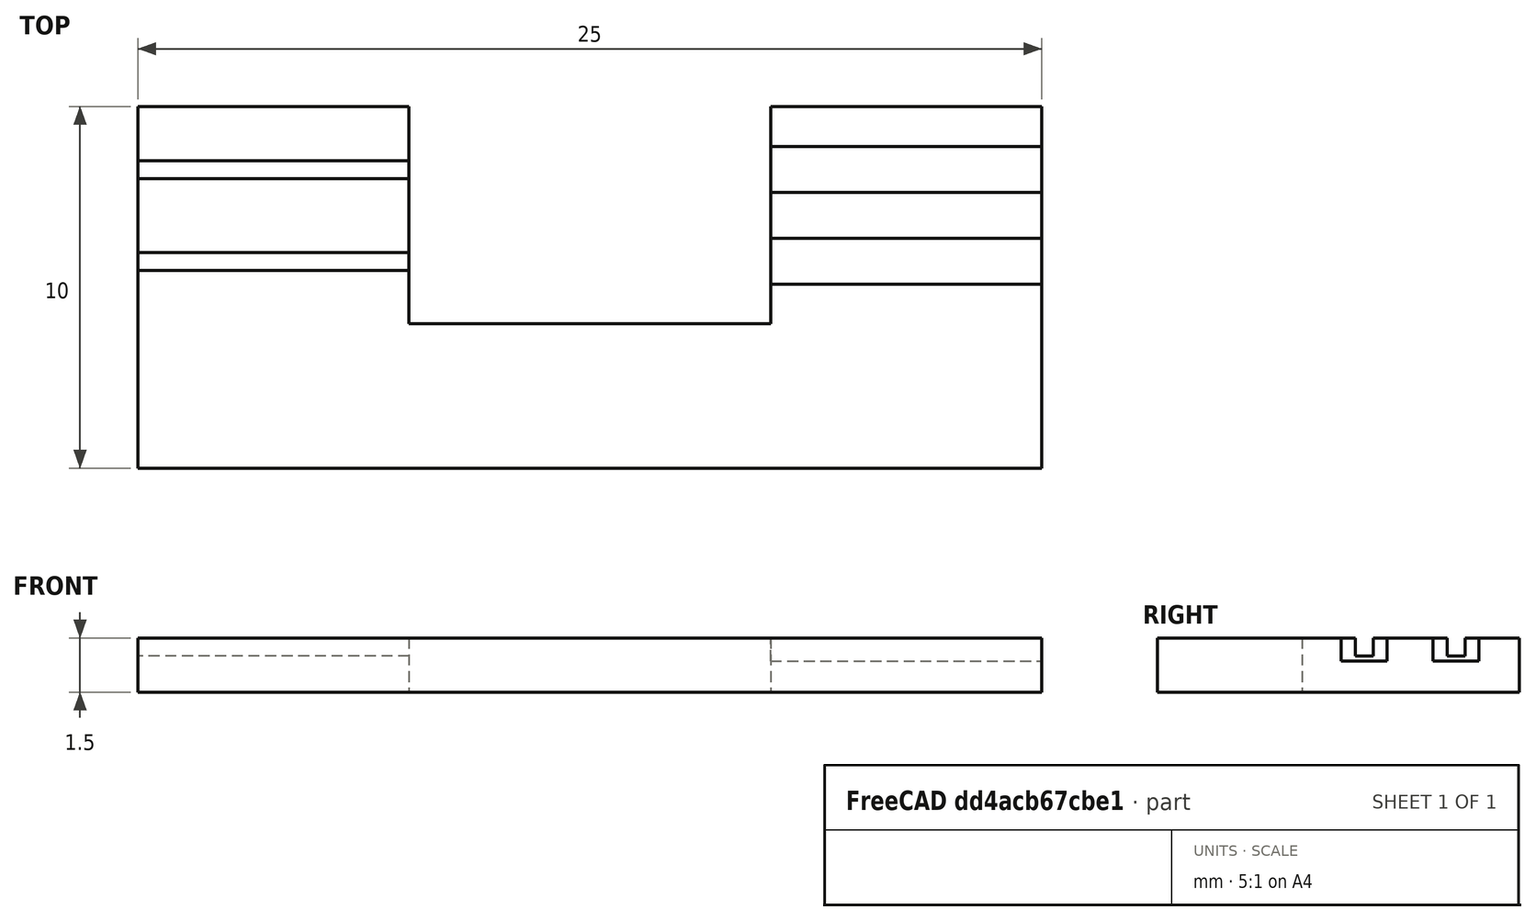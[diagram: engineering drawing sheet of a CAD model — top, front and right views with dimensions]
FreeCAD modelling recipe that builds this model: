
FCSTD DOCUMENT  (FreeCAD 0.18R16146 (Git))
Label: wire-jig
License: All rights reserved
LicenseURL: http://en.wikipedia.org/wiki/All_rights_reserved
objects: Sketcher::SketchObject×3, PartDesign::Pocket×2, PartDesign::Pad×1, PartDesign::Body×1
note: 10 computed .brp shape members not serialized (recipe doc carries the construction recipe); baked Part::Feature solids carry a one-line shape summary decoded from their .brp

FEATURE [Sketcher::SketchObject] Sketch
  MapMode = 5
  Support = -> [XY_Plane]
  sketch-geometry (8):
    g0: LineSegment StartX=-12.5 StartY=6 StartZ=0 EndX=-5 EndY=6 EndZ=0
    g1: LineSegment StartX=12.5 StartY=6 StartZ=0 EndX=12.5 EndY=-4 EndZ=0
    g2: LineSegment StartX=12.5 StartY=-4 StartZ=0 EndX=-12.5 EndY=-4 EndZ=0
    g3: LineSegment StartX=-12.5 StartY=-4 StartZ=0 EndX=-12.5 EndY=6 EndZ=0
    g4: LineSegment StartX=-5 StartY=6 StartZ=0 EndX=-5 EndY=0 EndZ=0
    g5: LineSegment StartX=-5 StartY=0 StartZ=0 EndX=5 EndY=0 EndZ=0
    g6: LineSegment StartX=5 StartY=0 StartZ=0 EndX=5 EndY=6 EndZ=0
    g7: LineSegment StartX=5 StartY=6 StartZ=0 EndX=12.5 EndY=6 EndZ=0
  constraints (22):
    c: Coincident(g7,g1)
    c: Coincident(g1,g2)
    c: Coincident(g2,g3)
    c: Coincident(g3,g0)
    c: Horizontal(g2)
    c: Vertical(g3)
    c: Symmetric(g0,g7,g-2)
    c: Vertical(g4)
    c: Coincident(g4,g5)
    c: Horizontal(g5)
    c: Coincident(g5,g6)
    c: Vertical(g6)
    c: PointOnObject(g5,g-1)
    c: Coincident(g0,g4)
    c: Tangent(g0,g7)
    c: Coincident(g6,g7)
    c: Equal(g0,g7)
    c: DistanceX(g0,g6) = 10
    c: Distance(g2) = 25
    c: Vertical(g1)
    c: Distance(g1) = 10
    c: DistanceY(g2,g4) = 4
FEATURE [PartDesign::Pad] Pad
  Length = 1.5
  Length2 = 100
  Profile = -> Sketch
  Reversed = true
  Type = 0
FEATURE [Sketcher::SketchObject] Sketch001
  MapMode = 5
  Support = -> [XY_Plane]
  sketch-geometry (11):
    g0: LineSegment StartX=-13.1646 StartY=4.50644 StartZ=0 EndX=-3.3788 EndY=4.50644 EndZ=0
    g1: LineSegment StartX=-3.3788 StartY=4.50644 StartZ=0 EndX=-3.3788 EndY=4.00644 EndZ=0
    g2: LineSegment StartX=-3.3788 StartY=4.00644 StartZ=0 EndX=-13.1646 EndY=4.00644 EndZ=0
    g3: LineSegment StartX=-13.1646 StartY=4.00644 StartZ=0 EndX=-13.1646 EndY=4.50644 EndZ=0
    g4: LineSegment StartX=-13.1646 StartY=1.96644 StartZ=0 EndX=-3.3788 EndY=1.96644 EndZ=0
    g5: LineSegment StartX=-3.3788 StartY=1.96644 StartZ=0 EndX=-3.3788 EndY=1.46644 EndZ=0
    g6: LineSegment StartX=-3.3788 StartY=1.46644 StartZ=0 EndX=-13.1646 EndY=1.46644 EndZ=0
    g7: LineSegment StartX=-13.1646 StartY=1.46644 StartZ=0 EndX=-13.1646 EndY=1.96644 EndZ=0
    g8: LineSegment StartX=3.29453 StartY=3.62144 StartZ=0 EndX=13.0803 EndY=3.62144 EndZ=0
    g9: LineSegment [constr] StartX=-13.9476 StartY=4.25644 StartZ=0 EndX=13.9476 EndY=4.25644 EndZ=0
    g10: LineSegment [constr] StartX=13.9476 StartY=1.71644 StartZ=0 EndX=-13.9476 EndY=1.71644 EndZ=0
  constraints (27):
    c: Coincident(g0,g1)
    c: Coincident(g1,g2)
    c: Coincident(g2,g3)
    c: Coincident(g3,g0)
    c: Horizontal(g0)
    c: Horizontal(g2)
    c: Vertical(g1)
    c: Coincident(g4,g5)
    c: Coincident(g5,g6)
    c: Coincident(g6,g7)
    c: Coincident(g7,g4)
    c: Horizontal(g4)
    c: Vertical(g5)
    c: Vertical(g7)
    c: Horizontal(g8)
    c: Equal(g3,g7)
    c: Symmetric(g9,g9,g-2)
    c: Vertical(g10,g9)
    c: Equal(g10,g9)
    c: Symmetric(g4,g6,g10)
    c: Symmetric(g2,g0,g9)
    c: Equal(g1,g5)
    c: Equal(g2,g4)
    c: Vertical(g4,g1)
    c: Equal(g2,g8)
    c: Distance(g3) = 0.5
    c: DistanceY(g10,g9) = 2.54
FEATURE [PartDesign::Body] Body
  Group = -> [Sketch,Pad,Sketch001,Sketch002,Pocket001,Pocket]
  Origin = -> Origin
  Tip = -> Pocket
FEATURE [Sketcher::SketchObject] Sketch002
  ExternalGeometry = -> [Pocket]
  MapMode = 5
  Support = -> [XY_Plane]
  sketch-geometry (10):
    g0: LineSegment StartX=13.4356 StartY=4.89144 StartZ=0 EndX=3.64684 EndY=4.89144 EndZ=0
    g1: LineSegment StartX=3.64684 StartY=4.89144 StartZ=0 EndX=3.64684 EndY=3.62144 EndZ=0
    g2: LineSegment StartX=3.64684 StartY=3.62144 StartZ=0 EndX=13.4356 EndY=3.62144 EndZ=0
    g3: LineSegment StartX=13.4356 StartY=3.62144 StartZ=0 EndX=13.4356 EndY=4.89144 EndZ=0
    g4: LineSegment StartX=13.4356 StartY=2.35144 StartZ=0 EndX=3.64684 EndY=2.35144 EndZ=0
    g5: LineSegment StartX=3.64684 StartY=2.35144 StartZ=0 EndX=3.64684 EndY=1.08144 EndZ=0
    g6: LineSegment StartX=3.64684 StartY=1.08144 StartZ=0 EndX=13.4356 EndY=1.08144 EndZ=0
    g7: LineSegment StartX=13.4356 StartY=1.08144 StartZ=0 EndX=13.4356 EndY=2.35144 EndZ=0
    g8: LineSegment [constr] StartX=-13.9476 StartY=4.25644 StartZ=0 EndX=13.9476 EndY=4.25644 EndZ=0
    g9: LineSegment [constr] StartX=13.9476 StartY=1.71644 StartZ=0 EndX=-13.9476 EndY=1.71644 EndZ=0
  constraints (25):
    c: Coincident(g0,g1)
    c: Coincident(g1,g2)
    c: Coincident(g2,g3)
    c: Coincident(g3,g0)
    c: Horizontal(g0)
    c: Horizontal(g2)
    c: Vertical(g1)
    c: Coincident(g4,g5)
    c: Coincident(g5,g6)
    c: Coincident(g6,g7)
    c: Coincident(g7,g4)
    c: Horizontal(g4)
    c: Vertical(g5)
    c: Equal(g3,g7)
    c: Symmetric(g8,g8,g-2)
    c: Vertical(g9,g8)
    c: Equal(g9,g8)
    c: Symmetric(g2,g0,g8)
    c: Symmetric(g4,g6,g9)
    c: Equal(g5,g1)
    c: Vertical(g1,g4)
    c: Equal(g2,g4)
    c: Distance(g3) = 1.27
    c: Symmetric(g-5,g-6,g9)
    c: Symmetric(g-4,g-3,g8)
FEATURE [PartDesign::Pocket] Pocket
  BaseFeature = -> Pocket001
  Length = 0.5
  Length2 = 100
  Profile = -> Sketch001
  Type = 0
FEATURE [PartDesign::Pocket] Pocket001
  BaseFeature = -> Pad
  Length = 0.635
  Length2 = 100
  Profile = -> Sketch002
  Type = 0
  expr: Length = 1.27 / 2
